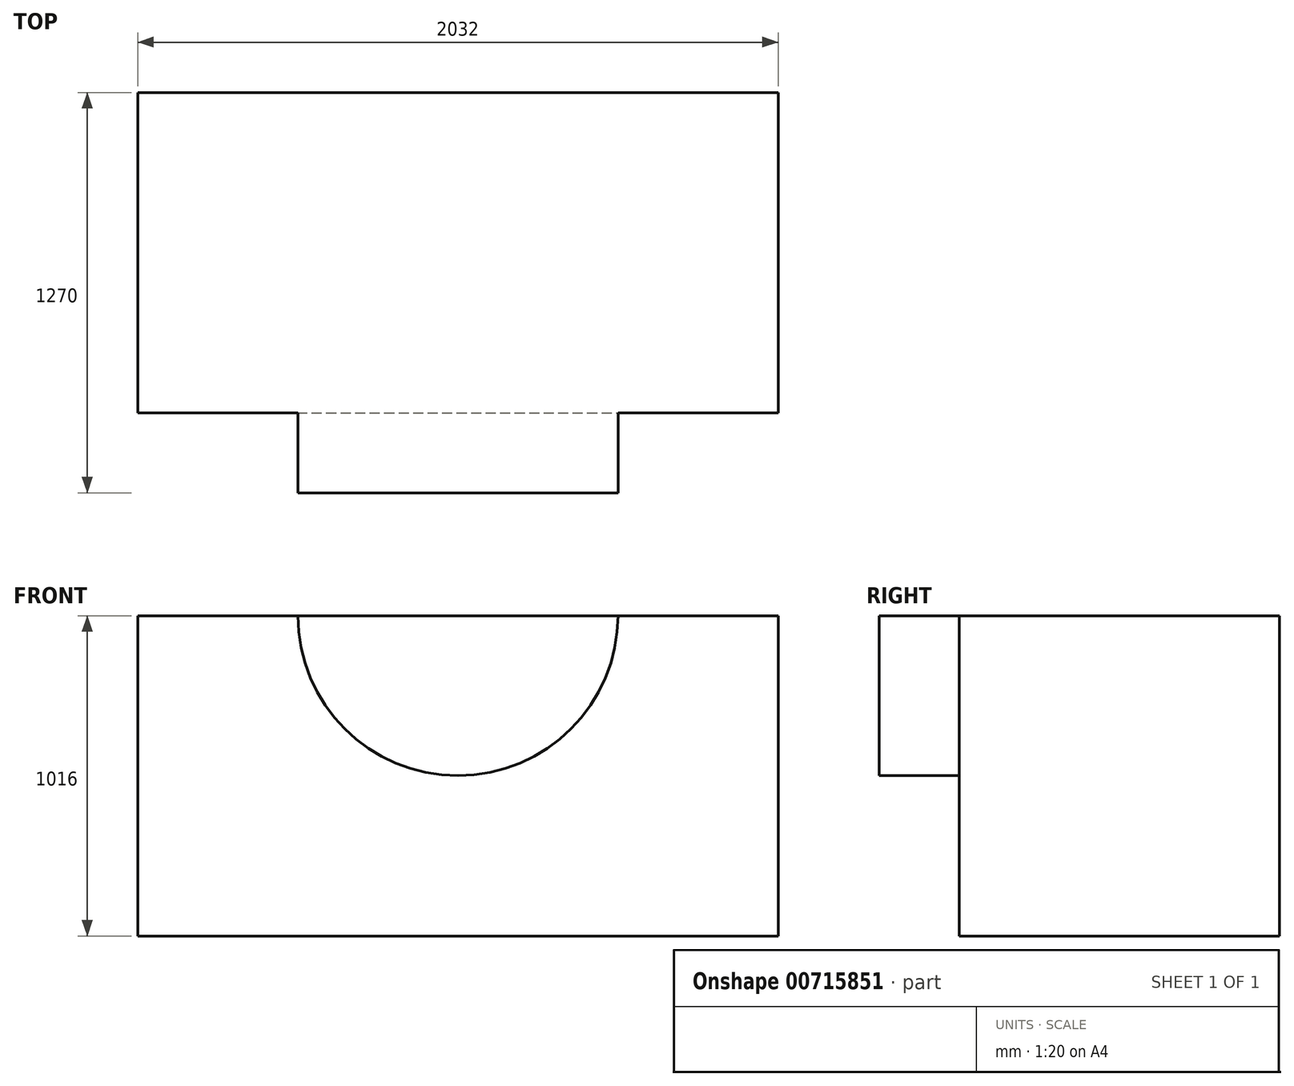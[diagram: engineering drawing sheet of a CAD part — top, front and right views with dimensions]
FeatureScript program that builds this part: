
annotation { "Feature Type Name" : "Feature", "Feature Type Description" : "" }
export const myFeature = defineFeature(function(context is Context, id is Id, definition is map)
    precondition{}
    {
        {
            var Q0;
            Q0=qCreatedBy(makeId("Top.planeOp"),FACE);
            var sketch = newSketch(context, id + "F0", { "sketchPlane" : qUnion([Q0])});
            skLineSegment(sketch, "E0.bottom", {"start": v(-1471.68, 707.96) * mm, "end": v(560.32, 707.96) * mm});
            skLineSegment(sketch, "E0.top", {"start": v(-1471.68, -308.04) * mm, "end": v(560.32, -308.04) * mm});
            skLineSegment(sketch, "E0.left", {"start": v(-1471.68, 707.96) * mm, "end": v(-1471.68, -308.04) * mm});
            skLineSegment(sketch, "E0.right", {"start": v(560.32, 707.96) * mm, "end": v(560.32, -308.04) * mm});
            skSolve(sketch);
        }
        {
            var Q0;
            Q0 = qSketchRegion(id + "F0", true);
            extrude(context, id + "F1", {"entities" : qUnion([Q0]), "depth" : 1016 * mm, "offsetDistance" : 25.4 * mm});
        }
        {
            var Q0;
            Q0=makeQuery(id+"F1.opExtrude","SWEPT_FACE",FACE,{"disambiguationData":[OSD([sQuery(id+"F0.wireOp",EDGE,"E0.top")])]});
            var sketch = newSketch(context, id + "F2", { "sketchPlane" : qUnion([Q0])});
            skArc(sketch, "E1", {"start": v(-963.68, 1016) * mm, "mid": v(-455.68, 508.74) * mm, "end": v(52.32, 1016) * mm});
            skLineSegment(sketch, "E2", {"start": v(-963.68, 1016) * mm, "end": v(-709.68, 1016) * mm});
            skLineSegment(sketch, "E3", {"start": v(52.32, 1016) * mm, "end": v(-201.68, 1016) * mm});
            skArc(sketch, "E4", {"start": v(-709.68, 1016) * mm, "mid": v(-455.68, 763.62) * mm, "end": v(-201.68, 1016) * mm});
            skSolve(sketch);
        }
        {
            var Q0;
            Q0 = qSketchRegion(id + "F2", true);
            var Q1;
            {var subQ0=sQuery(id+"F2.wireOp",EDGE,"E4");Q1=makeQuery(id+"F2.imprint","IMPRINT",FACE,{"disambiguationData":[TD([[makeQuery(id+"F2.imprint","IMPRINT",EDGE,{"derivedFrom":subQ0}),1.0]])]});}
            extrude(context, id + "F3", {"entities" : qUnion([Q0, Q1]), "operationType" : NewBodyOperationType.ADD, "depth" : 254 * mm, "offsetDistance" : 25.4 * mm});
        }
        {
            var Q0;
            Q0=makeQuery(id+"F3.opExtrude","CAP_FACE",FACE,{"disambiguationData":[OSD([sQuery(id+"F0.wireOp",EDGE,"E0.top"),sQuery(id+"F2.wireOp",EDGE,"E1"),sQuery(id+"F2.wireOp",EDGE,"E2"),sQuery(id+"F2.wireOp",EDGE,"E3")])],"isStart":false});
            var sketch = newSketch(context, id + "F4", { "sketchPlane" : qUnion([Q0])});
            skArc(sketch, "E5", {"start": v(-709.68, 1016) * mm, "mid": v(-455.68, 763.33) * mm, "end": v(-201.68, 1016) * mm});
            skLineSegment(sketch, "E6", {"start": v(-709.68, 1016) * mm, "end": v(-201.68, 1016) * mm});
            skSolve(sketch);
        }
        {
            var Q0;
            Q0 = qSketchRegion(id + "F4", true);
            extrude(context, id + "F5", {"entities" : qUnion([Q0]), "operationType" : NewBodyOperationType.ADD, "oppositeDirection" : true, "depth" : 1016 * mm, "offsetDistance" : 25.4 * mm});
        }
    });
